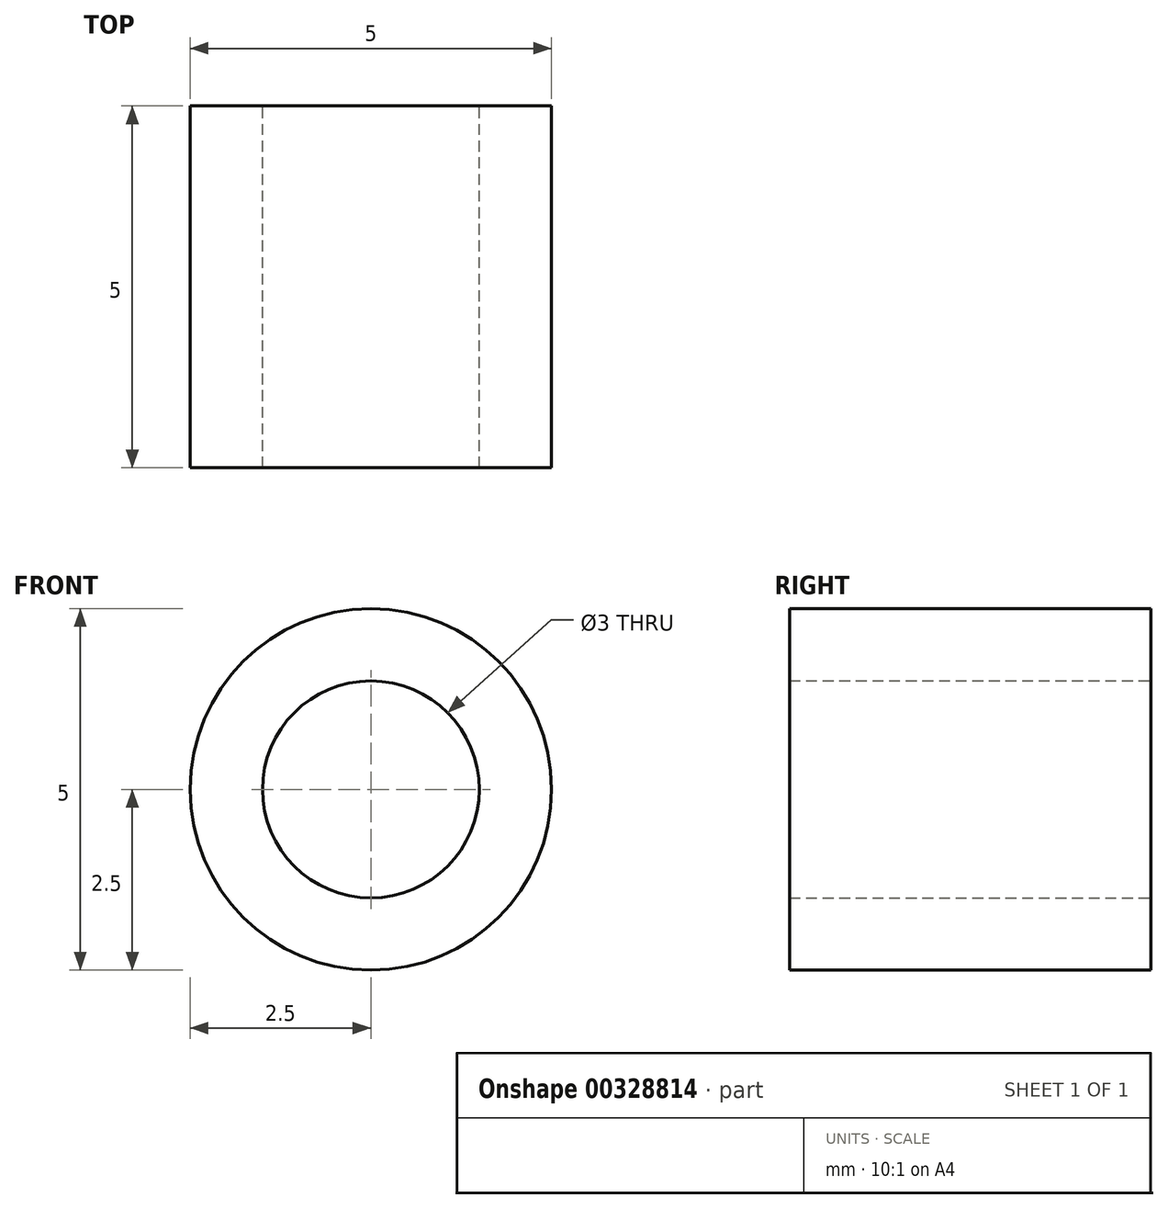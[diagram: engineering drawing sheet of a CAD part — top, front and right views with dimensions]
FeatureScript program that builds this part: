
annotation { "Feature Type Name" : "Feature", "Feature Type Description" : "" }
export const myFeature = defineFeature(function(context is Context, id is Id, definition is map)
    precondition{}
    {
        {
            var Q0;
            Q0=qCreatedBy(makeId("Front.planeOp"),FACE);
            var sketch = newSketch(context, id + "F0", { "sketchPlane" : qUnion([Q0])});
            skCircle(sketch, "E0", {"center": v(0, 0) * mm, "radius": 2.5 * mm});
            skCircle(sketch, "E1", {"center": v(0, 0) * mm, "radius": 1.5 * mm});
            skSolve(sketch);
        }
        {
            var Q0;
            Q0 = qSketchRegion(id + "F0", true);
            extrude(context, id + "F1", {"entities" : qUnion([Q0]), "depth" : 5 * mm});
        }
    });
